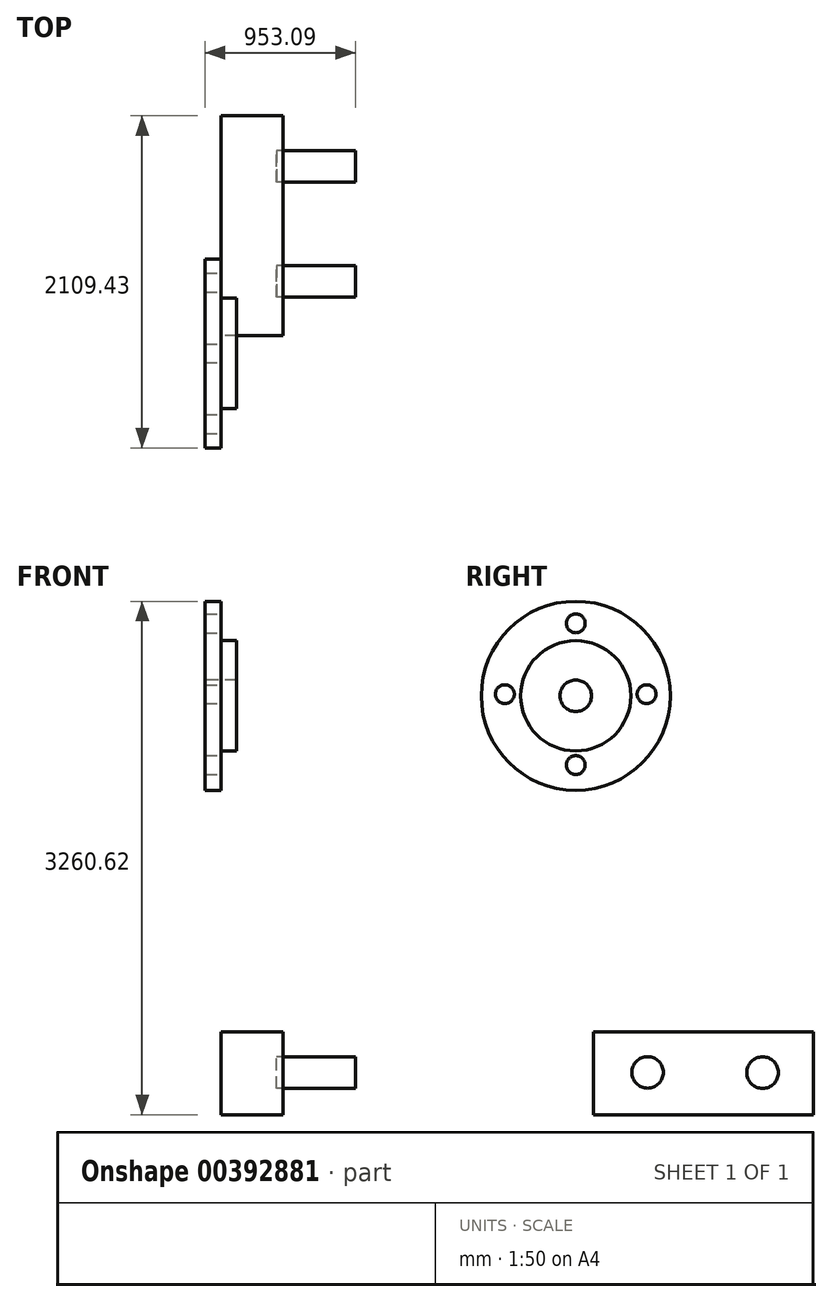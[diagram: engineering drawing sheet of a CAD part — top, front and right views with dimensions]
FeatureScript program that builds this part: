
annotation { "Feature Type Name" : "Feature", "Feature Type Description" : "" }
export const myFeature = defineFeature(function(context is Context, id is Id, definition is map)
    precondition{}
    {
        {
            var Q0;
            Q0=qCreatedBy(makeId("Front.planeOp"),FACE);
            var sketch = newSketch(context, id + "F0", { "sketchPlane" : qUnion([Q0])});
            skLineSegment(sketch, "E0", {"start": v(-453.09, 589.84) * mm, "end": v(-453.09, 89.84) * mm});
            skLineSegment(sketch, "E1", {"start": v(-453.09, 89.84) * mm, "end": v(-353.09, 89.84) * mm});
            skLineSegment(sketch, "E2", {"start": v(-353.09, 89.84) * mm, "end": v(-353.09, 589.84) * mm});
            skLineSegment(sketch, "E3", {"start": v(-353.09, 589.84) * mm, "end": v(-453.09, 589.84) * mm});
            skLineSegment(sketch, "E4.bottom", {"start": v(-353.09, 89.84) * mm, "end": v(-253.09, 89.84) * mm});
            skLineSegment(sketch, "E4.top", {"start": v(-353.09, 339.84) * mm, "end": v(-253.09, 339.84) * mm});
            skLineSegment(sketch, "E4.left", {"start": v(-353.09, 89.84) * mm, "end": v(-353.09, 339.84) * mm});
            skLineSegment(sketch, "E4.right", {"start": v(-253.09, 89.84) * mm, "end": v(-253.09, 339.84) * mm});
            skLineSegment(sketch, "E5", {"start": v(-549.73, -10.16) * mm, "end": v(-98.6, -10.16) * mm});
            skSolve(sketch);
        }
        {
            var Q0;
            Q0 = qSketchRegion(id + "F0", true);
            var Q1;
            Q1=sQuery(id+"F0.wireOp",EDGE,"E5");
            revolve(context, id + "F1", {"entities" : qUnion([Q0]), "axis" : qUnion([Q1]), "revolveType" : RevolveType.FULL});
        }
        {
            var Q0;
            Q0=makeQuery(id+"F1.opRevolve","SWEPT_FACE",FACE,{"disambiguationData":[OSD([sQuery(id+"F0.wireOp",EDGE,"E2")])]});
            var sketch = newSketch(context, id + "F2", { "sketchPlane" : qUnion([Q0])});
            skCircle(sketch, "E6", {"center": v(-450, 0) * mm, "radius": 60 * mm});
            skCircle(sketch, "E7.1.0", {"center": v(0, -450) * mm, "radius": 60 * mm});
            skCircle(sketch, "E7.2.0", {"center": v(450, 0) * mm, "radius": 60 * mm});
            skCircle(sketch, "E7.3.0", {"center": v(0, 450) * mm, "radius": 60 * mm});
            skPoint(sketch, "E7.center", {"position": v(0, 0) * mm});
            skSolve(sketch);
        }
        {
            var Q0;
            Q0=makeQuery(id+"F2.imprint","IMPRINT",FACE,{"disambiguationData":[TD([[makeQuery(id+"F2.imprint","IMPRINT",EDGE,{"derivedFrom":sQuery(id+"F2.wireOp",EDGE,"E6")}),1.0]])]});
            var Q1;
            Q1=makeQuery(id+"F2.imprint","IMPRINT",FACE,{"disambiguationData":[TD([[makeQuery(id+"F2.imprint","IMPRINT",EDGE,{"derivedFrom":sQuery(id+"F2.wireOp",EDGE,"E7.3.0")}),1.0]])]});
            var Q2;
            Q2=makeQuery(id+"F2.imprint","IMPRINT",FACE,{"disambiguationData":[TD([[makeQuery(id+"F2.imprint","IMPRINT",EDGE,{"derivedFrom":sQuery(id+"F2.wireOp",EDGE,"E7.1.0")}),1.0]])]});
            var Q3;
            Q3=makeQuery(id+"F2.imprint","IMPRINT",FACE,{"disambiguationData":[TD([[makeQuery(id+"F2.imprint","IMPRINT",EDGE,{"derivedFrom":sQuery(id+"F2.wireOp",EDGE,"E7.2.0")}),1.0]])]});
            extrude(context, id + "F3", {"entities" : qUnion([Q0, Q1, Q2, Q3]), "operationType" : NewBodyOperationType.REMOVE, "endBound" : BoundingType.THROUGH_ALL, "oppositeDirection" : true, "depth" : 25 * mm});
        }
        {
            var Q0;
            Q0=qCreatedBy(makeId("Right.planeOp"),FACE);
            var sketch = newSketch(context, id + "F4", { "sketchPlane" : qUnion([Q0])});
            skLineSegment(sketch, "E8", {"start": v(285.24, -2211.3) * mm, "end": v(1432.96, -2211.3) * mm});
            skLineSegment(sketch, "E9", {"start": v(1432.96, -2211.3) * mm, "end": v(1432.96, -2568.13) * mm});
            skLineSegment(sketch, "E10", {"start": v(1432.96, -2568.13) * mm, "end": v(285.24, -2568.13) * mm});
            skLineSegment(sketch, "E11", {"start": v(285.24, -2568.13) * mm, "end": v(285.24, -2211.3) * mm});
            skCircle(sketch, "E12", {"center": v(456.48, -2402.17) * mm, "radius": 100 * mm});
            skCircle(sketch, "E13", {"center": v(1186.67, -2403.78) * mm, "radius": 100 * mm});
            skSolve(sketch);
        }
        {
            var Q0;
            Q0=makeQuery(id+"F4.imprint","IMPRINT",FACE,{"disambiguationData":[TD([[makeQuery(id+"F4.imprint","IMPRINT",EDGE,{"derivedFrom":sQuery(id+"F4.wireOp",EDGE,"E12")}),1.0]])]});
            var sketch = newSketch(context, id + "F5", { "sketchPlane" : qUnion([Q0])});
            skSolve(sketch);
        }
        {
            var Q0;
            Q0=makeQuery(id+"F4.imprint","IMPRINT",FACE,{"disambiguationData":[TD([[makeQuery(id+"F4.imprint","IMPRINT",EDGE,{"derivedFrom":sQuery(id+"F4.wireOp",EDGE,"E13")}),1.0]])]});
            var Q1;
            Q1=makeQuery(id+"F5.imprint","IMPRINT",FACE,{"disambiguationData":[TD([[makeQuery(id+"F5.imprint","IMPRINT",EDGE,{"derivedFrom":makeQuery(id+"F4.imprint","IMPRINT",EDGE,{"derivedFrom":sQuery(id+"F4.wireOp",EDGE,"E12")})}),1.0]])]});
            extrude(context, id + "F6", {"entities" : qUnion([Q0, Q1]), "depth" : 500 * mm});
        }
        {
            var Q0;
            Q0=makeQuery(id+"F1.opRevolve","SWEPT_FACE",FACE,{"disambiguationData":[OSD([sQuery(id+"F0.wireOp",EDGE,"E2")])]});
            var sketch = newSketch(context, id + "F7", { "sketchPlane" : qUnion([Q0])});
            skLineSegment(sketch, "E14.bottom", {"start": v(113.65, -2143.68) * mm, "end": v(1509.43, -2143.68) * mm});
            skLineSegment(sketch, "E14.top", {"start": v(113.65, -2670.78) * mm, "end": v(1509.43, -2670.78) * mm});
            skLineSegment(sketch, "E14.left", {"start": v(113.65, -2143.68) * mm, "end": v(113.65, -2670.78) * mm});
            skLineSegment(sketch, "E14.right", {"start": v(1509.43, -2143.68) * mm, "end": v(1509.43, -2670.78) * mm});
            skSolve(sketch);
        }
        {
            var Q0;
            Q0=makeQuery(id+"F7.imprint","IMPRINT",FACE,{"disambiguationData":[TD([[makeQuery(id+"F7.imprint","IMPRINT",EDGE,{"derivedFrom":sQuery(id+"F7.wireOp",EDGE,"E14.bottom")}),-1.0]])]});
            extrude(context, id + "F8", {"entities" : qUnion([Q0]), "depth" : 392.91 * mm});
        }
    });
